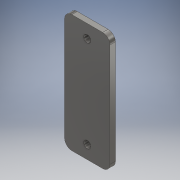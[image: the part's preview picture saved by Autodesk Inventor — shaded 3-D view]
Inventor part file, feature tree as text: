
AUTODESK INVENTOR PART (.ipt)
format: ipt  version: 2018 (Build 220112000, 112)  size: 118,272 bytes
history: native  units: mm
features: extrude x2, sketch x2, fillet x1
ambient origin geometry x8: Origin, YZ Plane, XZ Plane, XY Plane, X Axis, Y Axis, Z Axis, Center Point
bodies: Body1 (feature_tree)
feature tree (5):
  extrude  "Extrusión3"  Depth=50.0mm
  extrude  "Extrusión4"  Depth=8.0mm
  fillet  "Empalme2"  Radius=8.0mm
  sketch  "Boceto3"  dims[d15=6.0mm d16=50.0mm]
  sketch  "Boceto4"  dims[d17=130.0mm d18=0.0mm d19=75.0mm d20=8.0mm d21=26.0mm d22=100.0mm d23=0.0mm d24=8.0mm]
